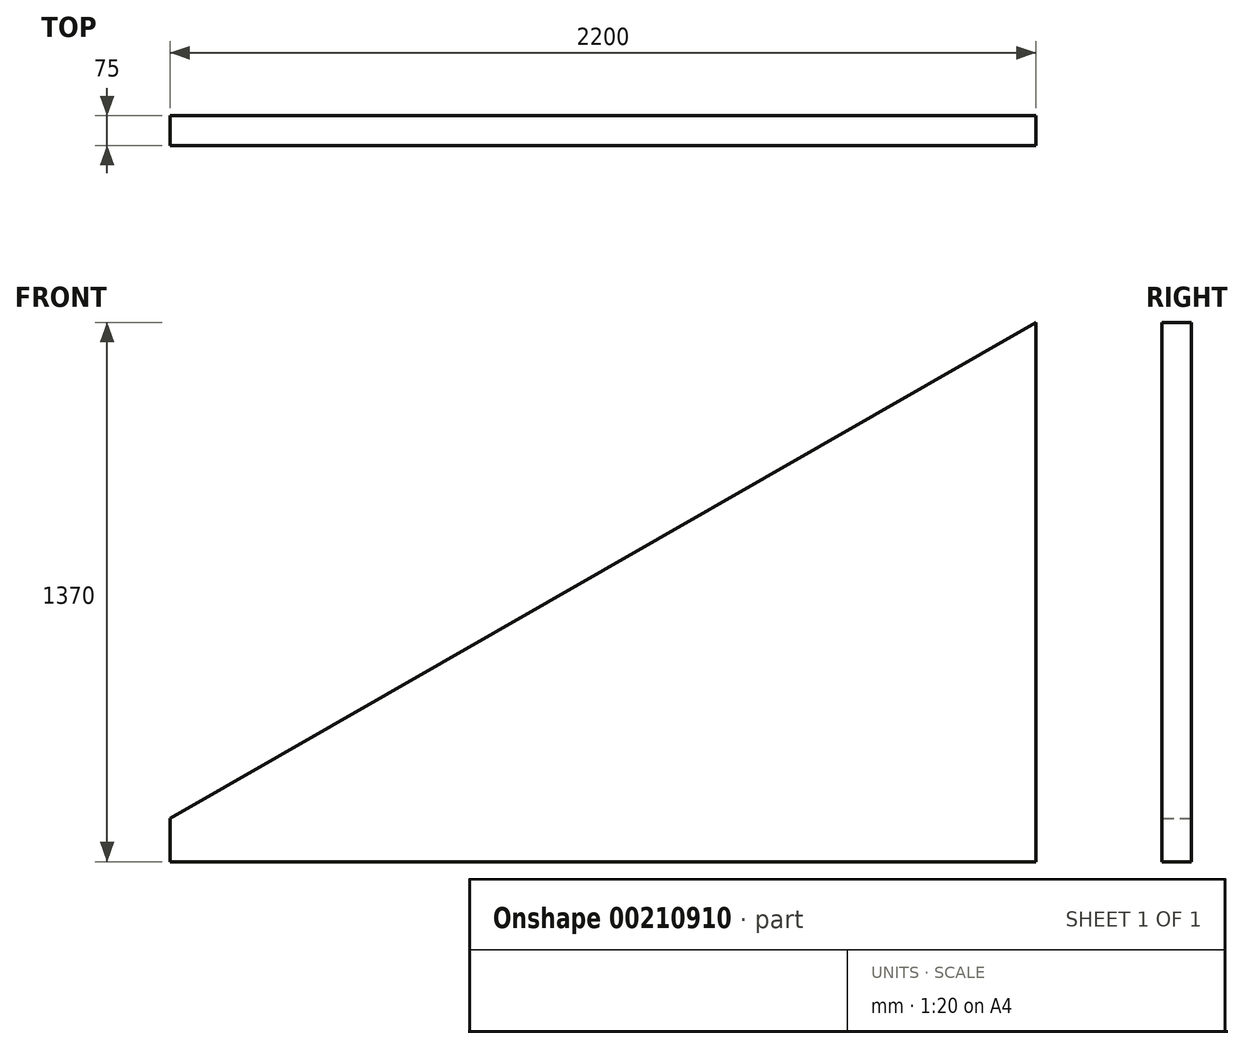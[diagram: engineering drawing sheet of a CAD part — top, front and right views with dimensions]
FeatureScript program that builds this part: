
annotation { "Feature Type Name" : "Feature", "Feature Type Description" : "" }
export const myFeature = defineFeature(function(context is Context, id is Id, definition is map)
    precondition{}
    {
        {
            var Q0;
            Q0=qCreatedBy(makeId("Front.planeOp"),FACE);
            var sketch = newSketch(context, id + "F0", { "sketchPlane" : qUnion([Q0])});
            skLineSegment(sketch, "E0.bottom", {"start": v(0, 0) * mm, "end": v(2200, 0) * mm});
            skLineSegment(sketch, "E0.right", {"start": v(2200, 0) * mm, "end": v(2200, 1370) * mm});
            skLineSegment(sketch, "E1", {"start": v(0, 110) * mm, "end": v(2200, 1370) * mm});
            skLineSegment(sketch, "E2", {"start": v(0, 0) * mm, "end": v(0, 110) * mm});
            skSolve(sketch);
        }
        {
            var Q0;
            Q0=makeQuery(id+"F0.imprint","IMPRINT",FACE,{"disambiguationData":[TD([[makeQuery(id+"F0.imprint","IMPRINT",EDGE,{"derivedFrom":sQuery(id+"F0.wireOp",EDGE,"E0.bottom")}),1.0]])]});
            extrude(context, id + "F1", {"entities" : qUnion([Q0]), "depth" : 75 * mm});
        }
    });
